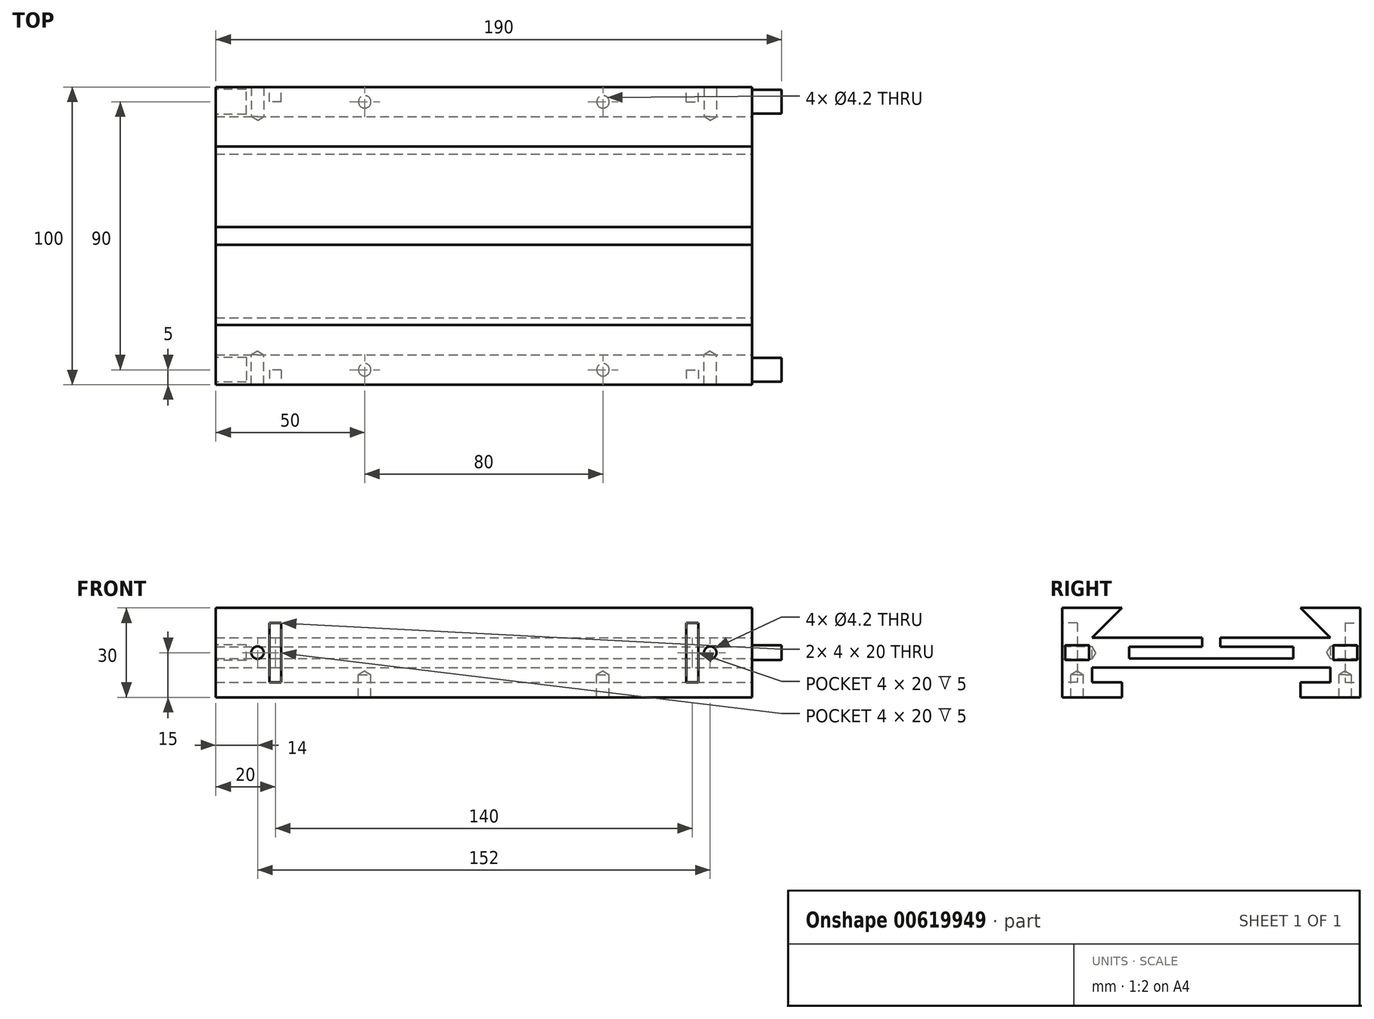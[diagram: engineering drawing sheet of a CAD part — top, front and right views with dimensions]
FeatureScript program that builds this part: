
annotation { "Feature Type Name" : "Feature", "Feature Type Description" : "" }
export const myFeature = defineFeature(function(context is Context, id is Id, definition is map)
    precondition{}
    {
        {
            var Q0;
            Q0=qCreatedBy(makeId("Top.planeOp"),FACE);
            var sketch = newSketch(context, id + "F0", { "sketchPlane" : qUnion([Q0])});
            skLineSegment(sketch, "E0.bottom", {"start": v(-90, 50) * mm, "end": v(90, 50) * mm});
            skLineSegment(sketch, "E0.top", {"start": v(-90, -50) * mm, "end": v(90, -50) * mm});
            skLineSegment(sketch, "E0.left", {"start": v(-90, 50) * mm, "end": v(-90, -50) * mm});
            skLineSegment(sketch, "E0.right", {"start": v(90, 50) * mm, "end": v(90, -50) * mm});
            skPoint(sketch, "E0.middle", {"position": v(0, 0) * mm});
            skSolve(sketch);
        }
        {
            var Q0;
            Q0=makeQuery(id+"F0.imprint","IMPRINT",FACE,{"disambiguationData":[TD([[makeQuery(id+"F0.imprint","IMPRINT",EDGE,{"derivedFrom":sQuery(id+"F0.wireOp",EDGE,"E0.bottom")}),-1.0]])]});
            extrude(context, id + "F1", {"entities" : qUnion([Q0]), "depth" : 30 * mm, "offsetDistance" : 25 * mm});
        }
        {
            var Q0;
            Q0=makeQuery(id+"F1.opExtrude","SWEPT_FACE",FACE,{"disambiguationData":[OSD([sQuery(id+"F0.wireOp",EDGE,"E0.right")])]});
            var sketch = newSketch(context, id + "F2", { "sketchPlane" : qUnion([Q0])});
            skPoint(sketch, "E1", {"position": v(-30, 30) * mm});
            skPoint(sketch, "E2", {"position": v(-40, 20) * mm});
            skPoint(sketch, "E3", {"position": v(40, 20) * mm});
            skPoint(sketch, "E4", {"position": v(30, 30) * mm});
            skPoint(sketch, "E5", {"position": v(-30, 0) * mm});
            skPoint(sketch, "E6", {"position": v(-30, 5) * mm});
            skPoint(sketch, "E7", {"position": v(-40, 5) * mm});
            skPoint(sketch, "E8", {"position": v(-40, 10) * mm});
            skPoint(sketch, "E9", {"position": v(40, 10) * mm});
            skPoint(sketch, "E10", {"position": v(40, 5) * mm});
            skPoint(sketch, "E11", {"position": v(30, 5) * mm});
            skPoint(sketch, "E12", {"position": v(30, 0) * mm});
            skLineSegment(sketch, "E13", {"start": v(-30, 30) * mm, "end": v(-40, 20) * mm});
            skLineSegment(sketch, "E14", {"start": v(-40, 20) * mm, "end": v(40, 20) * mm});
            skLineSegment(sketch, "E15", {"start": v(30, 30) * mm, "end": v(40, 20) * mm});
            skLineSegment(sketch, "E16", {"start": v(30, 30) * mm, "end": v(-30, 30) * mm});
            skLineSegment(sketch, "E17", {"start": v(-30, 0) * mm, "end": v(-30, 5) * mm});
            skLineSegment(sketch, "E18", {"start": v(-40, 5) * mm, "end": v(-40, 10) * mm});
            skLineSegment(sketch, "E19", {"start": v(-30, 5) * mm, "end": v(-40, 5) * mm});
            skLineSegment(sketch, "E20", {"start": v(-40, 10) * mm, "end": v(40, 10) * mm});
            skLineSegment(sketch, "E21", {"start": v(40, 10) * mm, "end": v(40, 5) * mm});
            skLineSegment(sketch, "E22", {"start": v(40, 5) * mm, "end": v(30, 5) * mm});
            skLineSegment(sketch, "E23", {"start": v(30, 0) * mm, "end": v(30, 5) * mm});
            skLineSegment(sketch, "E24", {"start": v(30, 0) * mm, "end": v(-30, 0) * mm});
            skPoint(sketch, "E25", {"position": v(0, 20) * mm});
            skPoint(sketch, "E26", {"position": v(3, 20) * mm});
            skPoint(sketch, "E27", {"position": v(-3, 20) * mm});
            skPoint(sketch, "E28", {"position": v(-27.5, 17) * mm});
            skPoint(sketch, "E29", {"position": v(-27.5, 13) * mm});
            skPoint(sketch, "E30", {"position": v(27.5, 13) * mm});
            skPoint(sketch, "E31", {"position": v(27.5, 17) * mm});
            skLineSegment(sketch, "E32", {"start": v(-3, 20) * mm, "end": v(-3, 17) * mm});
            skLineSegment(sketch, "E33", {"start": v(-3, 17) * mm, "end": v(-27.5, 17) * mm});
            skLineSegment(sketch, "E34", {"start": v(-27.5, 13) * mm, "end": v(27.5, 13) * mm});
            skLineSegment(sketch, "E35", {"start": v(27.5, 13) * mm, "end": v(27.5, 17) * mm});
            skLineSegment(sketch, "E36", {"start": v(27.5, 17) * mm, "end": v(3, 17) * mm});
            skLineSegment(sketch, "E37", {"start": v(3, 17) * mm, "end": v(3, 20) * mm});
            skLineSegment(sketch, "E38", {"start": v(3, 20) * mm, "end": v(-3, 20) * mm});
            skLineSegment(sketch, "E39", {"start": v(-27.5, 17) * mm, "end": v(-27.5, 13) * mm});
            skSolve(sketch);
        }
        {
            var Q0;
            Q0=makeQuery(id+"F2.imprint","IMPRINT",FACE,{"disambiguationData":[TD([[makeQuery(id+"F2.imprint","IMPRINT",EDGE,{"derivedFrom":sQuery(id+"F2.wireOp",EDGE,"E13")}),1.0]])]});
            var Q1;
            Q1=makeQuery(id+"F2.imprint","IMPRINT",FACE,{"disambiguationData":[TD([[makeQuery(id+"F2.imprint","IMPRINT",EDGE,{"derivedFrom":sQuery(id+"F2.wireOp",EDGE,"E17")}),-1.0]])]});
            var Q2;
            Q2=makeQuery(id+"F2.imprint","IMPRINT",FACE,{"disambiguationData":[TD([[makeQuery(id+"F2.imprint","IMPRINT",EDGE,{"derivedFrom":sQuery(id+"F2.wireOp",EDGE,"E32")}),1.0]])]});
            extrude(context, id + "F3", {"entities" : qUnion([Q0, Q1, Q2]), "operationType" : NewBodyOperationType.REMOVE, "oppositeDirection" : true, "depth" : 180 * mm, "offsetDistance" : 25 * mm});
        }
        {
            var Q0;
            Q0=makeQuery(id+"F1.opExtrude","SWEPT_FACE",FACE,{"disambiguationData":[OSD([sQuery(id+"F0.wireOp",EDGE,"E0.right")])]});
            var sketch = newSketch(context, id + "F4", { "sketchPlane" : qUnion([Q0])});
            skPoint(sketch, "E40", {"position": v(-45, 15) * mm});
            skPoint(sketch, "E41", {"position": v(45, 15) * mm});
            skLineSegment(sketch, "E42.bottom", {"start": v(-41, 12.5) * mm, "end": v(-49, 12.5) * mm});
            skLineSegment(sketch, "E42.top", {"start": v(-41, 17.5) * mm, "end": v(-49, 17.5) * mm});
            skLineSegment(sketch, "E42.left", {"start": v(-41, 12.5) * mm, "end": v(-41, 17.5) * mm});
            skLineSegment(sketch, "E42.right", {"start": v(-49, 12.5) * mm, "end": v(-49, 17.5) * mm});
            skLineSegment(sketch, "E43.bottom", {"start": v(41, 12.5) * mm, "end": v(49, 12.5) * mm});
            skLineSegment(sketch, "E43.top", {"start": v(41, 17.5) * mm, "end": v(49, 17.5) * mm});
            skLineSegment(sketch, "E43.left", {"start": v(41, 12.5) * mm, "end": v(41, 17.5) * mm});
            skLineSegment(sketch, "E43.right", {"start": v(49, 12.5) * mm, "end": v(49, 17.5) * mm});
            skSolve(sketch);
        }
        {
            var Q0;
            Q0=makeQuery(id+"F4.imprint","IMPRINT",FACE,{"disambiguationData":[TD([[makeQuery(id+"F4.imprint","IMPRINT",EDGE,{"derivedFrom":sQuery(id+"F4.wireOp",EDGE,"E42.bottom")}),-1.0]])]});
            var Q1;
            Q1=makeQuery(id+"F4.imprint","IMPRINT",FACE,{"disambiguationData":[TD([[makeQuery(id+"F4.imprint","IMPRINT",EDGE,{"derivedFrom":sQuery(id+"F4.wireOp",EDGE,"E43.bottom")}),1.0]])]});
            extrude(context, id + "F5", {"entities" : qUnion([Q0, Q1]), "operationType" : NewBodyOperationType.ADD, "depth" : 10 * mm, "offsetDistance" : 25 * mm});
        }
        {
            var Q0;
            Q0=makeQuery(id+"F1.opExtrude","SWEPT_FACE",FACE,{"disambiguationData":[OSD([sQuery(id+"F0.wireOp",EDGE,"E0.left")])]});
            var sketch = newSketch(context, id + "F6", { "sketchPlane" : qUnion([Q0])});
            skPoint(sketch, "E44", {"position": v(-45, 15) * mm});
            skPoint(sketch, "E44.positionSnap0", {"position": v(-50, 15) * mm});
            skPoint(sketch, "E45", {"position": v(45, 15) * mm});
            skLineSegment(sketch, "E46.bottom", {"start": v(-40.85, 12.35) * mm, "end": v(-49.15, 12.35) * mm});
            skLineSegment(sketch, "E46.top", {"start": v(-40.85, 17.65) * mm, "end": v(-49.15, 17.65) * mm});
            skLineSegment(sketch, "E46.left", {"start": v(-40.85, 12.35) * mm, "end": v(-40.85, 17.65) * mm});
            skLineSegment(sketch, "E46.right", {"start": v(-49.15, 12.35) * mm, "end": v(-49.15, 17.65) * mm});
            skLineSegment(sketch, "E47.bottom", {"start": v(40.85, 12.35) * mm, "end": v(49.15, 12.35) * mm});
            skLineSegment(sketch, "E47.top", {"start": v(40.85, 17.65) * mm, "end": v(49.15, 17.65) * mm});
            skLineSegment(sketch, "E47.left", {"start": v(40.85, 12.35) * mm, "end": v(40.85, 17.65) * mm});
            skLineSegment(sketch, "E47.right", {"start": v(49.15, 12.35) * mm, "end": v(49.15, 17.65) * mm});
            skSolve(sketch);
        }
        {
            var Q0;
            Q0=makeQuery(id+"F6.imprint","IMPRINT",FACE,{"disambiguationData":[TD([[makeQuery(id+"F6.imprint","IMPRINT",EDGE,{"derivedFrom":sQuery(id+"F6.wireOp",EDGE,"E46.bottom")}),-1.0]])]});
            var Q1;
            Q1=makeQuery(id+"F6.imprint","IMPRINT",FACE,{"disambiguationData":[TD([[makeQuery(id+"F6.imprint","IMPRINT",EDGE,{"derivedFrom":sQuery(id+"F6.wireOp",EDGE,"E47.bottom")}),1.0]])]});
            extrude(context, id + "F7", {"entities" : qUnion([Q0, Q1]), "operationType" : NewBodyOperationType.REMOVE, "oppositeDirection" : true, "depth" : 10.2 * mm, "offsetDistance" : 25 * mm});
        }
        {
            var Q0;
            Q0=makeQuery(id+"F1.opExtrude","SWEPT_FACE",FACE,{"disambiguationData":[OSD([sQuery(id+"F0.wireOp",EDGE,"E0.top")])]});
            var sketch = newSketch(context, id + "F8", { "sketchPlane" : qUnion([Q0])});
            skPoint(sketch, "E48", {"position": v(-70, 15) * mm});
            skLineSegment(sketch, "E49.bottom", {"start": v(-68, 25) * mm, "end": v(-72, 25) * mm});
            skLineSegment(sketch, "E49.top", {"start": v(-68, 5) * mm, "end": v(-72, 5) * mm});
            skLineSegment(sketch, "E49.left", {"start": v(-68, 25) * mm, "end": v(-68, 5) * mm});
            skLineSegment(sketch, "E49.right", {"start": v(-72, 25) * mm, "end": v(-72, 5) * mm});
            skLineSegment(sketch, "E50", {"start": v(0, 0) * mm, "end": v(0, 30) * mm, "construction": true});
            skLineSegment(sketch, "E51.MirrorCS", {"start": v(68, 25) * mm, "end": v(68, 5) * mm});
            skLineSegment(sketch, "E52.MirrorCS", {"start": v(72, 25) * mm, "end": v(72, 5) * mm});
            skLineSegment(sketch, "E53.MirrorCS", {"start": v(68, 25) * mm, "end": v(72, 25) * mm});
            skLineSegment(sketch, "E54.MirrorCS", {"start": v(68, 5) * mm, "end": v(72, 5) * mm});
            skPoint(sketch, "E55", {"position": v(-76, 15) * mm});
            skPoint(sketch, "E56.MirrorP", {"position": v(76, 15) * mm});
            skSolve(sketch);
        }
        {
            var Q0;
            Q0=makeQuery(id+"F8.imprint","IMPRINT",FACE,{"disambiguationData":[TD([[makeQuery(id+"F8.imprint","IMPRINT",EDGE,{"derivedFrom":sQuery(id+"F8.wireOp",EDGE,"E49.bottom")}),1.0]])]});
            var Q1;
            Q1=makeQuery(id+"F8.imprint","IMPRINT",FACE,{"disambiguationData":[TD([[makeQuery(id+"F8.imprint","IMPRINT",EDGE,{"derivedFrom":sQuery(id+"F8.wireOp",EDGE,"E51.MirrorCS")}),1.0]])]});
            extrude(context, id + "F9", {"entities" : qUnion([Q0, Q1]), "operationType" : NewBodyOperationType.REMOVE, "oppositeDirection" : true, "depth" : 5 * mm, "offsetDistance" : 25 * mm});
        }
        {
            var Q0;
            Q0=makeQuery(id+"F1.opExtrude","SWEPT_FACE",FACE,{"disambiguationData":[OSD([sQuery(id+"F0.wireOp",EDGE,"E0.bottom")])]});
            var sketch = newSketch(context, id + "F10", { "sketchPlane" : qUnion([Q0])});
            skPoint(sketch, "E57", {"position": v(70, 15) * mm});
            skLineSegment(sketch, "E58.bottom", {"start": v(68, 25) * mm, "end": v(72, 25) * mm});
            skLineSegment(sketch, "E58.top", {"start": v(68, 5) * mm, "end": v(72, 5) * mm});
            skLineSegment(sketch, "E58.left", {"start": v(68, 25) * mm, "end": v(68, 5) * mm});
            skLineSegment(sketch, "E58.right", {"start": v(72, 25) * mm, "end": v(72, 5) * mm});
            skLineSegment(sketch, "E59", {"start": v(0, 0) * mm, "end": v(0, 30) * mm, "construction": true});
            skLineSegment(sketch, "E60.MirrorCS", {"start": v(-68, 25) * mm, "end": v(-68, 5) * mm});
            skLineSegment(sketch, "E61.MirrorCS", {"start": v(-68, 25) * mm, "end": v(-72, 25) * mm});
            skLineSegment(sketch, "E62.MirrorCS", {"start": v(-72, 25) * mm, "end": v(-72, 5) * mm});
            skLineSegment(sketch, "E63.MirrorCS", {"start": v(-68, 5) * mm, "end": v(-72, 5) * mm});
            skPoint(sketch, "E64", {"position": v(76, 15) * mm});
            skPoint(sketch, "E65.MirrorP", {"position": v(-76, 15) * mm});
            skSolve(sketch);
        }
        {
            var Q0;
            Q0 = qSketchRegion(id + "F10", true);
            extrude(context, id + "F11", {"entities" : qUnion([Q0]), "operationType" : NewBodyOperationType.REMOVE, "oppositeDirection" : true, "depth" : 5 * mm, "offsetDistance" : 25 * mm});
        }
        {
            var Q0;
            Q0=sQuery(id+"F8.wireOp",VERTEX,"E55");
            var Q1;
            Q1=sQuery(id+"F8.wireOp",VERTEX,"E56.MirrorP");
            var Q2;
            Q2=makeQuery(id+"F1.opExtrude","SWEPT_BODY",BODY,{"disambiguationData":[OSD([sQuery(id+"F0.wireOp",EDGE,"E0.bottom"),sQuery(id+"F0.wireOp",EDGE,"E0.top"),sQuery(id+"F0.wireOp",EDGE,"E0.left"),sQuery(id+"F0.wireOp",EDGE,"E0.right")])]});
            hole(context, id + "F12", {"style" : HoleStyle.SIMPLE, "endStyle" : HoleEndStyle.BLIND, "standardTappedOrClearance" : lookupTablePath({ "standard" : "ISO", "engagement" : "75%", "pitch" : "0.8 mm", "size" : "M5", "type" : "Tapped" }), "standardBlindInLast" : lookupTablePath({ "standard" : "ISO", "engagement" : "75%", "pitch" : "0.8 mm", "size" : "M5", "type" : "Tapped" }), "holeDiameter" : 4.2 * mm, "majorDiameter" : 5 * mm, "showTappedDepth" : true, "holeDepth" : 10 * mm, "isTappedThrough" : true, "tappedDepth" : 7.6 * mm, "tapClearance" : 3, "locations" : qUnion([Q0, Q1]), "scope" : qUnion([Q2]), "startStyle" : HoleStartStyle.SKETCH});
        }
        {
            var Q0;
            Q0=sQuery(id+"F10.wireOp",VERTEX,"E65.MirrorP");
            var Q1;
            Q1=sQuery(id+"F10.wireOp",VERTEX,"E64");
            var Q2;
            Q2=makeQuery(id+"F1.opExtrude","SWEPT_BODY",BODY,{"disambiguationData":[OSD([sQuery(id+"F0.wireOp",EDGE,"E0.bottom"),sQuery(id+"F0.wireOp",EDGE,"E0.top"),sQuery(id+"F0.wireOp",EDGE,"E0.left"),sQuery(id+"F0.wireOp",EDGE,"E0.right")])]});
            hole(context, id + "F13", {"style" : HoleStyle.SIMPLE, "endStyle" : HoleEndStyle.BLIND, "standardTappedOrClearance" : lookupTablePath({ "standard" : "ISO", "engagement" : "75%", "pitch" : "0.8 mm", "size" : "M5", "type" : "Tapped" }), "standardBlindInLast" : lookupTablePath({ "standard" : "ISO", "engagement" : "75%", "pitch" : "0.8 mm", "size" : "M5", "type" : "Tapped" }), "holeDiameter" : 4.2 * mm, "majorDiameter" : 5 * mm, "showTappedDepth" : true, "holeDepth" : 10 * mm, "isTappedThrough" : true, "tappedDepth" : 7.6 * mm, "tapClearance" : 3, "locations" : qUnion([Q0, Q1]), "scope" : qUnion([Q2]), "startStyle" : HoleStartStyle.SKETCH});
        }
        {
            var Q0;
            {var subQ0=sQuery(id+"F0.wireOp",EDGE,"E0.bottom");var subQ1=sQuery(id+"F0.wireOp",EDGE,"E0.right");var subQ2=sQuery(id+"F0.wireOp",EDGE,"E0.left");Q0=makeQuery(id+"F3.boolean.opBoolean","SPLIT",FACE,{"disambiguationData":[TD([makeQuery(id+"F1.opExtrude","SWEPT_FACE",FACE,{"disambiguationData":[OSD([subQ0])]})])],"derivedFrom":makeQuery(id+"F1.opExtrude","CAP_FACE",FACE,{"disambiguationData":[OSD([subQ0,sQuery(id+"F0.wireOp",EDGE,"E0.top"),subQ2,subQ1])],"isStart":true})});}
            var sketch = newSketch(context, id + "F14", { "sketchPlane" : qUnion([Q0])});
            skPoint(sketch, "E66", {"position": v(40, 45) * mm});
            skLineSegment(sketch, "E67", {"start": v(0, -50) * mm, "end": v(0, 50.08) * mm, "construction": true});
            skPoint(sketch, "E67.endSnap0", {"position": v(0, -50) * mm});
            skLineSegment(sketch, "E68", {"start": v(0, 0) * mm, "end": v(89.96, 0) * mm, "construction": true});
            skPoint(sketch, "E69.MirrorP", {"position": v(40, -45) * mm});
            skLineSegment(sketch, "E70.MirrorCS", {"start": v(0, 50) * mm, "end": v(0, -50.08) * mm, "construction": true});
            skPoint(sketch, "E71.MirrorP", {"position": v(-40, 45) * mm});
            skPoint(sketch, "E72.MirrorP", {"position": v(-40, -45) * mm});
            skSolve(sketch);
        }
        {
            var Q0;
            Q0=sQuery(id+"F14.wireOp",VERTEX,"E71.MirrorP");
            var Q1;
            Q1=sQuery(id+"F14.wireOp",VERTEX,"E66");
            var Q2;
            Q2=sQuery(id+"F14.wireOp",VERTEX,"E69.MirrorP");
            var Q3;
            Q3=sQuery(id+"F14.wireOp",VERTEX,"E72.MirrorP");
            var Q4;
            Q4=makeQuery(id+"F1.opExtrude","SWEPT_BODY",BODY,{"disambiguationData":[OSD([sQuery(id+"F0.wireOp",EDGE,"E0.bottom"),sQuery(id+"F0.wireOp",EDGE,"E0.top"),sQuery(id+"F0.wireOp",EDGE,"E0.left"),sQuery(id+"F0.wireOp",EDGE,"E0.right")])]});
            hole(context, id + "F15", {"style" : HoleStyle.SIMPLE, "endStyle" : HoleEndStyle.BLIND, "standardTappedOrClearance" : lookupTablePath({ "standard" : "ISO", "engagement" : "75%", "pitch" : "0.8 mm", "size" : "M5", "type" : "Tapped" }), "standardBlindInLast" : lookupTablePath({ "standard" : "ISO", "engagement" : "75%", "pitch" : "0.8 mm", "size" : "M5", "type" : "Tapped" }), "holeDiameter" : 4.2 * mm, "majorDiameter" : 5 * mm, "showTappedDepth" : true, "holeDepth" : 7.6 * mm, "isTappedThrough" : true, "tappedDepth" : 7.6 * mm, "tapClearance" : 0, "locations" : qUnion([Q0, Q1, Q2, Q3]), "scope" : qUnion([Q4]), "startStyle" : HoleStartStyle.SKETCH});
        }
    });
